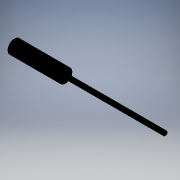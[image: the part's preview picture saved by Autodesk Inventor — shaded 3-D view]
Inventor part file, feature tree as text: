
AUTODESK INVENTOR PART (.ipt)
format: ipt  version: 2017.3 (Build 213256000, 256)  size: 143,872 bytes
history: native  units: mm (DEFAULTED — no unit token found)
features: other x91, revolve x3, sketch x3
ambient origin geometry x8: Origin, YZ Plane, XZ Plane, XY Plane, X Axis, Y Axis, Z Axis, Center Point
bodies: Solid1 (feature_tree)
feature tree (97):
  revolve  "Revolution1"  Angle=360.0deg
  revolve  "Revolution2"  [1 undecoded]
  revolve  "Revolution3"  [1 undecoded]
  other  "dia1_XY"
  other  "dia1_YZ"
  other  "dia1_ZX"
  other  "dia1_X"
  other  "dia1_Y"
  other  "dia1_Z"
  other  "dia1_Center"
  other  "dia12_XY"
  other  "dia12_YZ"
  other  "dia12_ZX"
  other  "dia12_X"
  other  "dia12_Y"
  other  "dia12_Z"
  other  "dia12_Center"
  other  "dia1r_XY"
  other  "dia1r_YZ"
  other  "dia1r_ZX"
  other  "dia1r_X"
  other  "dia1r_Y"
  other  "dia1r_Z"
  other  "dia1r_Center"
  other  "dia2_XY"
  other  "dia2_YZ"
  other  "dia2_ZX"
  other  "dia2_X"
  other  "dia2_Y"
  other  "dia2_Z"
  other  "dia2_Center"
  other  "dia22_XY"
  other  "dia22_YZ"
  other  "dia22_ZX"
  other  "dia22_X"
  other  "dia22_Y"
  other  "dia22_Z"
  other  "dia22_Center"
  other  "dia2r_XY"
  other  "dia2r_YZ"
  other  "dia2r_ZX"
  other  "dia2r_X"
  other  "dia2r_Y"
  other  "dia2r_Z"
  other  "dia2r_Center"
  other  "rl1_XY"
  other  "rl1_YZ"
  other  "rl1_ZX"
  other  "rl1_X"
  other  "rl1_Y"
  other  "rl1_Z"
  other  "rl1_Center"
  other  "rl2_XY"
  other  "rl2_YZ"
  other  "rl2_ZX"
  other  "rl2_X"
  other  "rl2_Y"
  other  "rl2_Z"
  other  "rl2_Center"
  other  "rod_cp_XY"
  other  "rod_cp_YZ"
  other  "rod_cp_ZX"
  other  "rod_cp_X"
  other  "rod_cp_Y"
  other  "rod_cp_Z"
  other  "rod_cp_Center"
  other  "stroke1_XY"
  other  "stroke1_YZ"
  other  "stroke1_ZX"
  other  "stroke1_X"
  other  "stroke1_Y"
  other  "stroke1_Z"
  other  "stroke1_Center"
  other  "thd1_XY"
  other  "thd1_YZ"
  other  "thd1_ZX"
  other  "thd1_X"
  other  "thd1_Y"
  other  "thd1_Z"
  other  "thd1_Center"
  other  "thd2_XY"
  other  "thd2_YZ"
  other  "thd2_ZX"
  other  "thd2_X"
  other  "thd2_Y"
  other  "thd2_Z"
  other  "thd2_Center"
  other  "to_rod_clevis_XY"
  other  "to_rod_clevis_YZ"
  other  "to_rod_clevis_ZX"
  other  "to_rod_clevis_X"
  other  "to_rod_clevis_Y"
  other  "to_rod_clevis_Z"
  other  "to_rod_clevis_Center"
  sketch  "Sketch_1"  dims[d0=360.0deg d1=360.0deg]
  sketch  "Sketch_3"  dims[d2=360.0deg]
  sketch  "Sketch_30"  dims[d3=0.0mm d4=0.0mm d5=0.0mm d6=0.0mm d7=0.0mm d8=0.0mm]
note: 2 required parameter values undecoded (feature->parameter linkage not recoverable at this tier; creation-order binding heuristic only, values carry confidence <= 0.55)
